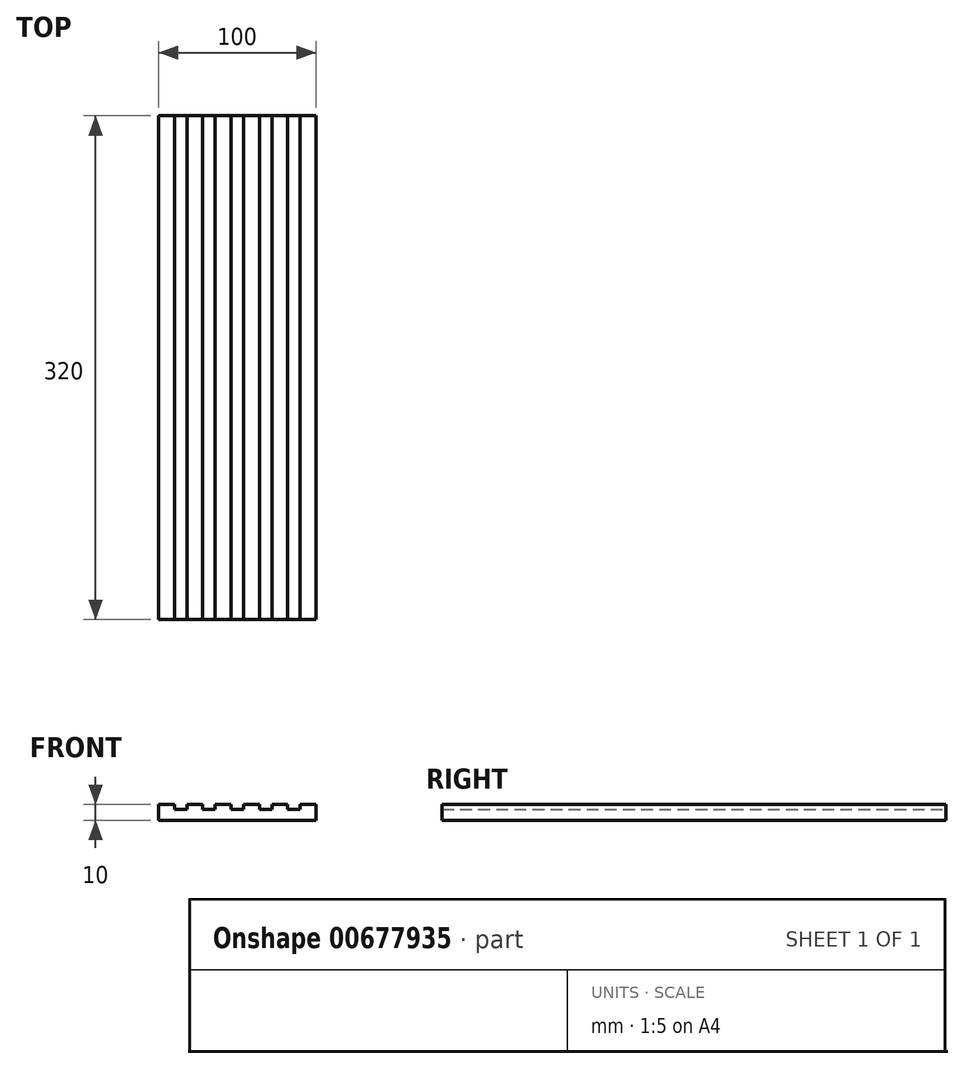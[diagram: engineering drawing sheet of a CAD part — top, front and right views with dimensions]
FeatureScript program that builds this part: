
annotation { "Feature Type Name" : "Feature", "Feature Type Description" : "" }
export const myFeature = defineFeature(function(context is Context, id is Id, definition is map)
    precondition{}
    {
        {
            var Q0;
            Q0=qCreatedBy(makeId("Front.planeOp"),FACE);
            var sketch = newSketch(context, id + "F0", { "sketchPlane" : qUnion([Q0])});
            skLineSegment(sketch, "E0.bottom", {"start": v(-50, 0) * mm, "end": v(-40, 0) * mm});
            skLineSegment(sketch, "E0.top", {"start": v(-50, -10) * mm, "end": v(50, -10) * mm});
            skLineSegment(sketch, "E0.left", {"start": v(-50, 0) * mm, "end": v(-50, -10) * mm});
            skLineSegment(sketch, "E0.right", {"start": v(50, 0) * mm, "end": v(50, -10) * mm});
            skLineSegment(sketch, "E1", {"start": v(-40, 0) * mm, "end": v(-40, -3) * mm});
            skLineSegment(sketch, "E2", {"start": v(-40, -3) * mm, "end": v(-32, -3) * mm});
            skLineSegment(sketch, "E3", {"start": v(-32, -3) * mm, "end": v(-32, 0) * mm});
            skLineSegment(sketch, "E4", {"start": v(-22, 0) * mm, "end": v(-22, -3) * mm});
            skLineSegment(sketch, "E5", {"start": v(-22, -3) * mm, "end": v(-14, -3) * mm});
            skLineSegment(sketch, "E6", {"start": v(-14, -3) * mm, "end": v(-14, 0) * mm});
            skLineSegment(sketch, "E7", {"start": v(-4, 0) * mm, "end": v(-4, -3) * mm});
            skLineSegment(sketch, "E8", {"start": v(-4, -3) * mm, "end": v(4, -3) * mm});
            skLineSegment(sketch, "E9", {"start": v(4, -3) * mm, "end": v(4, 0) * mm});
            skLineSegment(sketch, "E10", {"start": v(14, 0) * mm, "end": v(14, -3) * mm});
            skLineSegment(sketch, "E11", {"start": v(14, -3) * mm, "end": v(22, -3) * mm});
            skLineSegment(sketch, "E12", {"start": v(22, -3) * mm, "end": v(22, 0) * mm});
            skLineSegment(sketch, "E13", {"start": v(32, 0) * mm, "end": v(32, -3) * mm});
            skLineSegment(sketch, "E14", {"start": v(32, -3) * mm, "end": v(40, -3) * mm});
            skLineSegment(sketch, "E15", {"start": v(40, -3) * mm, "end": v(40, 0) * mm});
            skLineSegment(sketch, "E16.trimOffspring", {"start": v(-32, 0) * mm, "end": v(-22, 0) * mm});
            skLineSegment(sketch, "E17.trimOffspring", {"start": v(-14, 0) * mm, "end": v(-4, 0) * mm});
            skLineSegment(sketch, "E18.trimOffspring", {"start": v(4, 0) * mm, "end": v(14, 0) * mm});
            skLineSegment(sketch, "E19.trimOffspring", {"start": v(22, 0) * mm, "end": v(32, 0) * mm});
            skLineSegment(sketch, "E20.trimOffspring", {"start": v(40, 0) * mm, "end": v(50, 0) * mm});
            skSolve(sketch);
        }
        {
            var Q0;
            Q0 = qSketchRegion(id + "F0", true);
            extrude(context, id + "F1", {"entities" : qUnion([Q0]), "depth" : 320 * mm, "offsetDistance" : 25 * mm});
        }
    });
